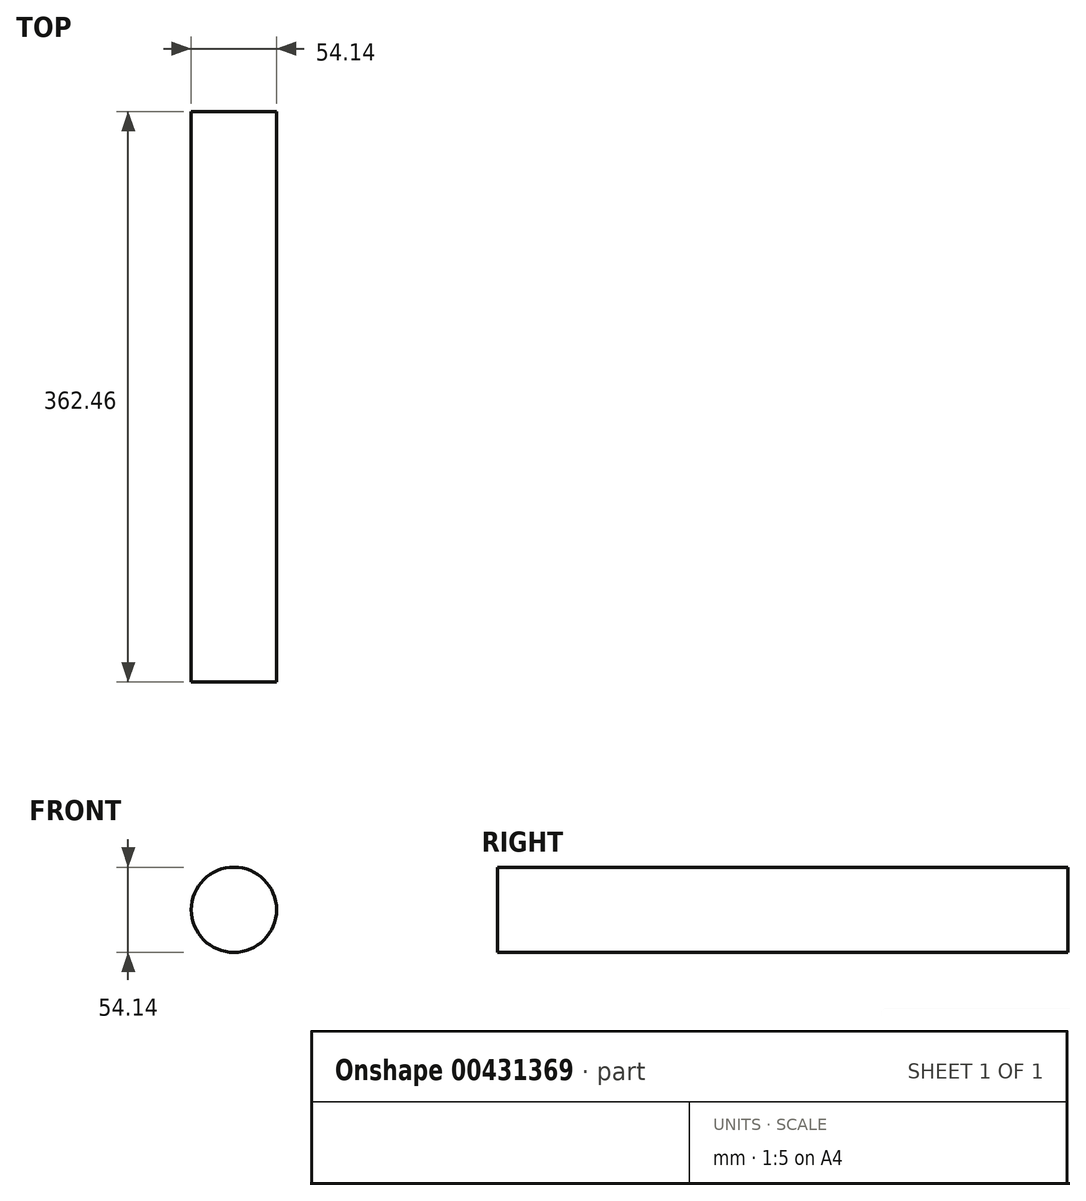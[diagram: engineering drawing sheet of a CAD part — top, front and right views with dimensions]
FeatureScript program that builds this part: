
annotation { "Feature Type Name" : "Feature", "Feature Type Description" : "" }
export const myFeature = defineFeature(function(context is Context, id is Id, definition is map)
    precondition{}
    {
        {
            var Q0;
            Q0=qCreatedBy(makeId("Front.planeOp"),FACE);
            var sketch = newSketch(context, id + "F0", { "sketchPlane" : qUnion([Q0])});
            skCircle(sketch, "E0", {"center": v(-37.88, 0) * mm, "radius": 27.07 * mm});
            skSolve(sketch);
        }
        {
            var Q0;
            Q0=sQuery(id+"F0.wireOp",EDGE,"E0");
            extrude(context, id + "F1", {"bodyType" : ToolBodyType.SURFACE, "surfaceEntities" : qUnion([Q0]), "depth" : 362.46 * mm});
        }
    });
